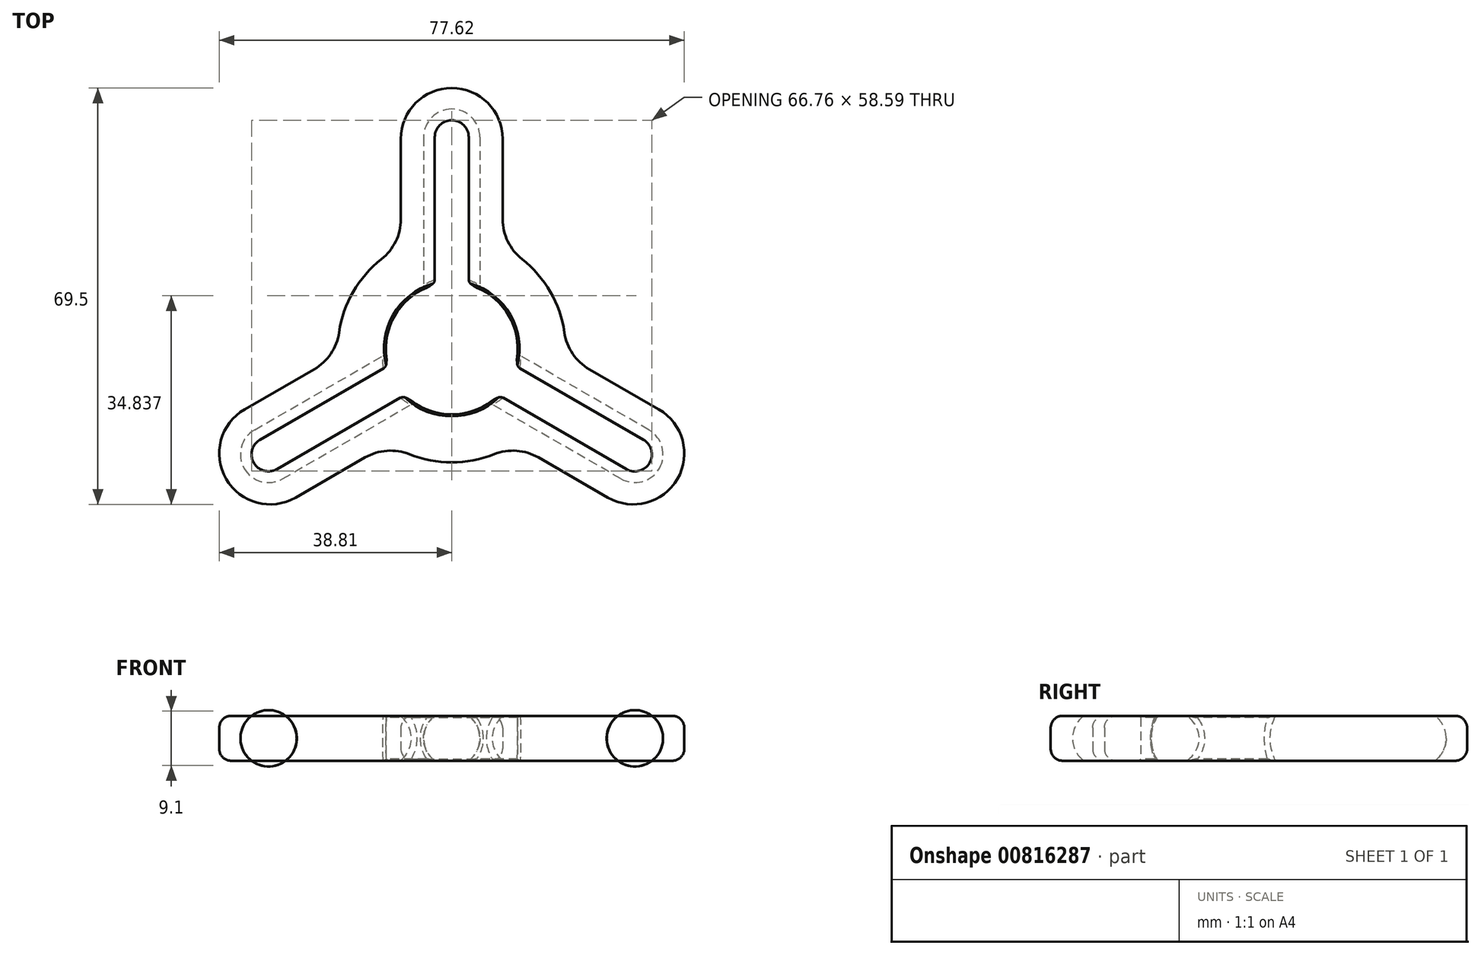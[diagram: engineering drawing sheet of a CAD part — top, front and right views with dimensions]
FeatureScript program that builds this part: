
annotation { "Feature Type Name" : "Feature", "Feature Type Description" : "" }
export const myFeature = defineFeature(function(context is Context, id is Id, definition is map)
    precondition{}
    {
        {
            var Q0;
            Q0=qCreatedBy(makeId("Top.planeOp"),FACE);
            var sketch = newSketch(context, id + "F0", { "sketchPlane" : qUnion([Q0])});
            skLineSegment(sketch, "E0", {"start": v(-9.53, 5.5) * mm, "end": v(0, 0) * mm, "construction": true});
            skLineSegment(sketch, "E1", {"start": v(0, 0) * mm, "end": v(9.53, 5.5) * mm, "construction": true});
            skArc(sketch, "E2", {"start": v(9.53, 5.5) * mm, "mid": v(0, 11) * mm, "end": v(-9.53, 5.5) * mm});
            skLineSegment(sketch, "E3", {"start": v(0, 0) * mm, "end": v(0, 11) * mm, "construction": true});
            skLineSegment(sketch, "E4", {"start": v(-9.53, 5.5) * mm, "end": v(-16.45, 9.5) * mm});
            skLineSegment(sketch, "E5", {"start": v(9.53, 5.5) * mm, "end": v(21.03, 12.14) * mm});
            skLineSegment(sketch, "E6", {"start": v(-8.5, 17) * mm, "end": v(-8.5, 35) * mm});
            skLineSegment(sketch, "E7", {"start": v(8.5, 35) * mm, "end": v(8.5, 17) * mm});
            skArc(sketch, "E8", {"start": v(-16.45, 9.5) * mm, "mid": v(-13.03, 13.83) * mm, "end": v(-8.5, 17) * mm});
            skArc(sketch, "E9", {"start": v(-8.5, 35) * mm, "mid": v(0, 43.5) * mm, "end": v(8.5, 35) * mm});
            skArc(sketch, "E10.trimOffspring", {"start": v(8.5, 17) * mm, "mid": v(13.03, 13.83) * mm, "end": v(16.45, 9.5) * mm});
            skSolve(sketch);
        }
        {
            var Q0;
            Q0 = qSketchRegion(id + "F0", true);
            extrude(context, id + "F1", {"entities" : qUnion([Q0]), "depth" : 3.75 * mm, "offsetDistance" : 25 * mm, "hasSecondDirection" : true, "secondDirectionOppositeDirection" : true, "secondDirectionDepth" : 3.75 * mm});
        }
        {
            var Q0;
            Q0=qCreatedBy(makeId("Front.planeOp"),FACE);
            var sketch = newSketch(context, id + "F2", { "sketchPlane" : qUnion([Q0])});
            skCircle(sketch, "E11", {"center": v(0, 0) * mm, "radius": 4.7 * mm});
            skSolve(sketch);
        }
        {
            var Q0;
            Q0 = qSketchRegion(id + "F2", true);
            extrude(context, id + "F3", {"entities" : qUnion([Q0]), "oppositeDirection" : true, "depth" : 40 * mm, "offsetDistance" : 25 * mm});
        }
        {
            var Q0;
            Q0=makeQuery(id+"F3.opExtrude","CAP_EDGE",EDGE,{"disambiguationData":[OSD([sQuery(id+"F2.wireOp",EDGE,"E11")])],"isStart":false});
            fillet(context, id + "F4", {"entities" : qUnion([Q0]), "radius" : 4.7 * mm, "tangentPropagation" : true, "allowEdgeOverflow" : false});
        }
        {
            var Q0;
            Q0=makeQuery(id+"F1.opExtrude","SWEPT_EDGE",EDGE,{"disambiguationData":[OSD([sQuery(id+"F0.wireOp",EDGE,"E6"),sQuery(id+"F0.wireOp",EDGE,"E8")])]});
            var Q1;
            Q1=makeQuery(id+"F1.opExtrude","SWEPT_EDGE",EDGE,{"disambiguationData":[OSD([sQuery(id+"F0.wireOp",EDGE,"E7"),sQuery(id+"F0.wireOp",EDGE,"E10.trimOffspring")])]});
            fillet(context, id + "F5", {"entities" : qUnion([Q0, Q1]), "radius" : 8.5 * mm, "tangentPropagation" : true, "allowEdgeOverflow" : false});
        }
        {
            var Q0;
            Q0=makeQuery(id+"F3.opExtrude","SWEPT_BODY",BODY,{"disambiguationData":[OSD([sQuery(id+"F2.wireOp",EDGE,"E11")])]});
            var Q1;
            Q1=makeQuery(id+"F1.opExtrude","SWEPT_BODY",BODY,{"disambiguationData":[OSD([sQuery(id+"F0.wireOp",EDGE,"E2"),sQuery(id+"F0.wireOp",EDGE,"E4"),sQuery(id+"F0.wireOp",EDGE,"E5"),sQuery(id+"F0.wireOp",EDGE,"E6"),sQuery(id+"F0.wireOp",EDGE,"E7"),sQuery(id+"F0.wireOp",EDGE,"E8"),sQuery(id+"F0.wireOp",EDGE,"E9"),sQuery(id+"F0.wireOp",EDGE,"E10.trimOffspring")])]});
            booleanBodies(context, id + "F6", {"operationType" : BooleanOperationType.SUBTRACTION, "tools" : qUnion([Q0]), "targets" : qUnion([Q1])});
        }
        {
            var Q0;
            {var subQ0=sQuery(id+"F0.wireOp",EDGE,"E2");var subQ1=sQuery(id+"F0.wireOp",EDGE,"E4");Q0=makeQuery(id+"F6.opBoolean","SPLIT",EDGE,{"disambiguationData":[TD([makeQuery(id+"F1.opExtrude","SWEPT_FACE",FACE,{"disambiguationData":[OSD([subQ1])]})])],"derivedFrom":makeQuery(id+"F1.opExtrude","CAP_EDGE",EDGE,{"disambiguationData":[OSD([subQ0])],"isStart":false})});}
            var Q1;
            {var subQ0=sQuery(id+"F0.wireOp",EDGE,"E2");var subQ1=sQuery(id+"F0.wireOp",EDGE,"E4");Q1=makeQuery(id+"F6.opBoolean","SPLIT",EDGE,{"disambiguationData":[TD([makeQuery(id+"F1.opExtrude","SWEPT_FACE",FACE,{"disambiguationData":[OSD([subQ1])]})])],"derivedFrom":makeQuery(id+"F1.opExtrude","CAP_EDGE",EDGE,{"disambiguationData":[OSD([subQ0])],"isStart":true})});}
            var Q2;
            {var subQ0=sQuery(id+"F0.wireOp",EDGE,"E2");var subQ1=sQuery(id+"F0.wireOp",EDGE,"E5");Q2=makeQuery(id+"F6.opBoolean","SPLIT",EDGE,{"disambiguationData":[TD([makeQuery(id+"F1.opExtrude","SWEPT_FACE",FACE,{"disambiguationData":[OSD([subQ1])]})])],"derivedFrom":makeQuery(id+"F1.opExtrude","CAP_EDGE",EDGE,{"disambiguationData":[OSD([subQ0])],"isStart":true})});}
            var Q3;
            {var subQ0=sQuery(id+"F0.wireOp",EDGE,"E2");var subQ1=sQuery(id+"F0.wireOp",EDGE,"E5");Q3=makeQuery(id+"F6.opBoolean","SPLIT",EDGE,{"disambiguationData":[TD([makeQuery(id+"F1.opExtrude","SWEPT_FACE",FACE,{"disambiguationData":[OSD([subQ1])]})])],"derivedFrom":makeQuery(id+"F1.opExtrude","CAP_EDGE",EDGE,{"disambiguationData":[OSD([subQ0])],"isStart":false})});}
            chamfer(context, id + "F7", {"entities" : qUnion([Q0, Q1, Q2, Q3]), "width" : 0.3 * mm, "tangentPropagation" : true});
        }
        {
            var Q0;
            Q0=makeQuery(id+"F6.opBoolean","INTERSECT",EDGE,{"disambiguationData":[OD(1.0)],"derivedFrom":[makeQuery(id+"F1.opExtrude","SWEPT_FACE",FACE,{"disambiguationData":[OSD([sQuery(id+"F0.wireOp",EDGE,"E2")])]}),makeQuery(id+"F3.opExtrude","SWEPT_FACE",FACE,{"disambiguationData":[OSD([sQuery(id+"F2.wireOp",EDGE,"E11")])]})]});
            var Q1;
            Q1=makeQuery(id+"F6.opBoolean","INTERSECT",EDGE,{"disambiguationData":[OD(0.0)],"derivedFrom":[makeQuery(id+"F1.opExtrude","SWEPT_FACE",FACE,{"disambiguationData":[OSD([sQuery(id+"F0.wireOp",EDGE,"E2")])]}),makeQuery(id+"F3.opExtrude","SWEPT_FACE",FACE,{"disambiguationData":[OSD([sQuery(id+"F2.wireOp",EDGE,"E11")])]})]});
            fillet(context, id + "F8", {"entities" : qUnion([Q0, Q1]), "radius" : 1 * mm, "tangentPropagation" : true, "allowEdgeOverflow" : false});
        }
        {
            var Q0;
            Q0=qCreatedBy(makeId("Front.planeOp"),FACE);
            var sketch = newSketch(context, id + "F9", { "sketchPlane" : qUnion([Q0])});
            skLineSegment(sketch, "E12", {"start": v(0, 0) * mm, "end": v(0, 24.93) * mm});
            skSolve(sketch);
        }
        {
            var Q0;
            Q0=makeQuery(id+"F1.opExtrude","SWEPT_BODY",BODY,{"disambiguationData":[OSD([sQuery(id+"F0.wireOp",EDGE,"E2"),sQuery(id+"F0.wireOp",EDGE,"E4"),sQuery(id+"F0.wireOp",EDGE,"E5"),sQuery(id+"F0.wireOp",EDGE,"E6"),sQuery(id+"F0.wireOp",EDGE,"E7"),sQuery(id+"F0.wireOp",EDGE,"E8"),sQuery(id+"F0.wireOp",EDGE,"E9"),sQuery(id+"F0.wireOp",EDGE,"E10.trimOffspring")])]});
            var Q1;
            Q1=sQuery(id+"F9.wireOp",EDGE,"E12");
            circularPattern(context, id + "F10", {"operationType" : NewBodyOperationType.ADD, "entities" : qUnion([Q0]), "axis" : qUnion([Q1]), "angle" : 360 * degree, "instanceCount" : 3, "equalSpace" : true});
        }
        {
            var Q0;
            Q0=makeQuery(id+"F1.opExtrude","CAP_EDGE",EDGE,{"disambiguationData":[OSD([sQuery(id+"F0.wireOp",EDGE,"E6")])],"isStart":false});
            var Q1;
            Q1=makeQuery(id+"F10.opPattern","COPY",EDGE,{"derivedFrom":makeQuery(id+"F1.opExtrude","CAP_EDGE",EDGE,{"disambiguationData":[OSD([sQuery(id+"F0.wireOp",EDGE,"E6")])],"isStart":true}),"instanceName":"1"});
            fillet(context, id + "F11", {"entities" : qUnion([Q0, Q1]), "radius" : 2 * mm, "tangentPropagation" : true, "allowEdgeOverflow" : false});
        }
    });
